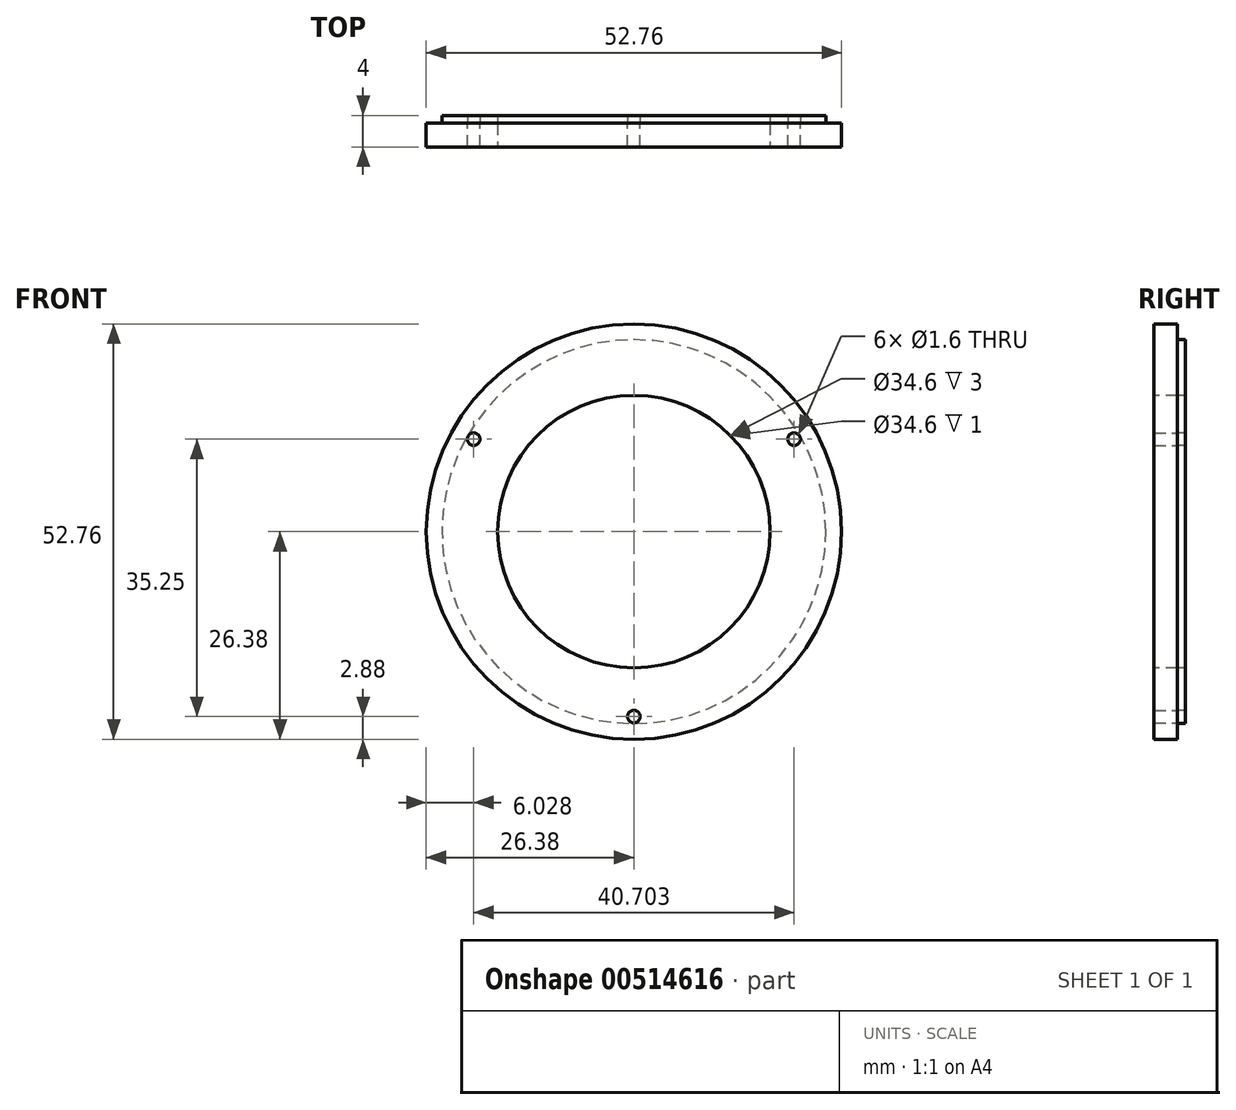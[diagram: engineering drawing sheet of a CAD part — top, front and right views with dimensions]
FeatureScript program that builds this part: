
annotation { "Feature Type Name" : "Feature", "Feature Type Description" : "" }
export const myFeature = defineFeature(function(context is Context, id is Id, definition is map)
    precondition{}
    {
        {
            var Q0;
            Q0=qCreatedBy(makeId("Front.planeOp"),FACE);
            var sketch = newSketch(context, id + "F0", { "sketchPlane" : qUnion([Q0])});
            skCircle(sketch, "E0", {"center": v(0, 0) * mm, "radius": 24.38 * mm});
            skSolve(sketch);
        }
        {
            var Q0;
            Q0 = qSketchRegion(id + "F0", true);
            extrude(context, id + "F1", {"entities" : qUnion([Q0]), "depth" : 1 * mm, "offsetDistance" : 25 * mm});
        }
        {
            var Q0;
            Q0=makeQuery(id+"F1.opExtrude","CAP_FACE",FACE,{"disambiguationData":[OSD([sQuery(id+"F0.wireOp",EDGE,"E0")])],"isStart":false});
            var sketch = newSketch(context, id + "F2", { "sketchPlane" : qUnion([Q0])});
            skCircle(sketch, "E1", {"center": v(0, 0) * mm, "radius": 26.38 * mm});
            skCircle(sketch, "E2", {"center": v(0, 0) * mm, "radius": 22.38 * mm});
            skLineSegment(sketch, "E3", {"start": v(0, 0) * mm, "end": v(0, -22.38) * mm});
            skCircle(sketch, "E4", {"center": v(0, 0) * mm, "radius": 23.5 * mm});
            skLineSegment(sketch, "E5", {"start": v(0, -22.38) * mm, "end": v(0, -23.5) * mm});
            skCircle(sketch, "E6", {"center": v(0, -23.5) * mm, "radius": 0.8 * mm});
            skCircle(sketch, "E7.1.0", {"center": v(20.35, 11.75) * mm, "radius": 0.8 * mm});
            skCircle(sketch, "E7.2.0", {"center": v(-20.35, 11.75) * mm, "radius": 0.8 * mm});
            skSolve(sketch);
        }
        {
            var Q0;
            Q0=makeQuery(id+"F2.imprint","IMPRINT",FACE,{"disambiguationData":[TD([[makeQuery(id+"F2.imprint","IMPRINT",EDGE,{"derivedFrom":sQuery(id+"F2.wireOp",EDGE,"E1")}),1.0]])]});
            var Q1;
            Q1=makeQuery(id+"F2.imprint","IMPRINT",FACE,{"disambiguationData":[TD([[makeQuery(id+"F2.imprint","IMPRINT",EDGE,{"derivedFrom":sQuery(id+"F2.wireOp",EDGE,"E2")}),1.0]])]});
            var Q2;
            Q2=makeQuery(id+"F2.imprint","IMPRINT",FACE,{"disambiguationData":[TD([[makeQuery(id+"F2.imprint","IMPRINT",EDGE,{"derivedFrom":sQuery(id+"F2.wireOp",EDGE,"E2")}),-1.0]])]});
            var Q3;
            Q3=makeQuery(id+"F2.imprint","IMPRINT",FACE,{"disambiguationData":[TD([[makeQuery(id+"F2.imprint","IMPRINT",EDGE,{"derivedFrom":makeQuery(id+"F1.opExtrude","CAP_EDGE",EDGE,{"disambiguationData":[OSD([sQuery(id+"F0.wireOp",EDGE,"E0")])],"isStart":false})}),1.0]])]});
            var Q4;
            Q4=sQuery(id+"F2.wireOp",EDGE,"E7.2.0");
            var Q5;
            Q5=sQuery(id+"F2.wireOp",EDGE,"E7.1.0");
            var Q6;
            Q6=sQuery(id+"F2.wireOp",EDGE,"E6");
            extrude(context, id + "F3", {"entities" : qUnion([Q0, Q1, Q2, Q3]), "surfaceEntities" : qUnion([Q4, Q5, Q6]), "depth" : 3 * mm, "offsetDistance" : 25 * mm});
        }
        {
            var Q0;
            Q0=makeQuery(id+"F3.opExtrude","CAP_FACE",FACE,{"disambiguationData":[OSD([sQuery(id+"F2.wireOp",EDGE,"E1"),sQuery(id+"F2.wireOp",EDGE,"E6"),sQuery(id+"F2.wireOp",EDGE,"E7.1.0"),sQuery(id+"F2.wireOp",EDGE,"E7.2.0")])],"isStart":false});
            var sketch = newSketch(context, id + "F4", { "sketchPlane" : qUnion([Q0])});
            skCircle(sketch, "E8", {"center": v(-20.35, 11.75) * mm, "radius": 0.8 * mm});
            skCircle(sketch, "E9", {"center": v(20.35, 11.75) * mm, "radius": 0.8 * mm});
            skCircle(sketch, "E10", {"center": v(0, -23.5) * mm, "radius": 0.8 * mm});
            skSolve(sketch);
        }
        {
            var Q0;
            Q0 = qSketchRegion(id + "F4", true);
            extrude(context, id + "F5", {"entities" : qUnion([Q0]), "operationType" : NewBodyOperationType.REMOVE, "oppositeDirection" : true, "depth" : 25 * mm, "offsetDistance" : 25 * mm});
        }
        {
            var Q0;
            Q0=makeQuery(id+"F3.opExtrude","CAP_FACE",FACE,{"disambiguationData":[OSD([sQuery(id+"F2.wireOp",EDGE,"E1"),sQuery(id+"F2.wireOp",EDGE,"E6"),sQuery(id+"F2.wireOp",EDGE,"E7.1.0"),sQuery(id+"F2.wireOp",EDGE,"E7.2.0")])],"isStart":false});
            var sketch = newSketch(context, id + "F6", { "sketchPlane" : qUnion([Q0])});
            skCircle(sketch, "E11", {"center": v(0, 0) * mm, "radius": 17.3 * mm});
            skSolve(sketch);
        }
        {
            var Q0;
            Q0 = qSketchRegion(id + "F6", true);
            extrude(context, id + "F7", {"entities" : qUnion([Q0]), "operationType" : NewBodyOperationType.REMOVE, "oppositeDirection" : true, "depth" : 25 * mm, "offsetDistance" : 25 * mm});
        }
    });
